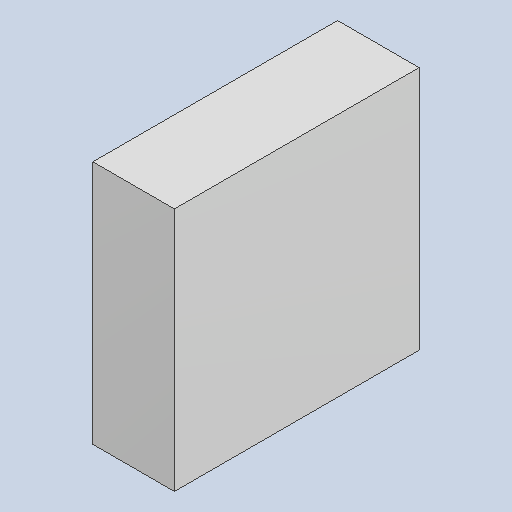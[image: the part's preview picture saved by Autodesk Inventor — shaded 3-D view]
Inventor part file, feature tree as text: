
AUTODESK INVENTOR PART (.ipt)
format: ipt  version: 2023.4 (Build 274418000, 418)  size: 81,408 bytes
history: native  units: mm
features: extrude x1
ambient origin geometry x8: Origin, YZ Plane, XZ Plane, XY Plane, X Axis, Y Axis, Z Axis, Center Point
bodies: Solid1 (feature_tree)
feature tree (1):
  extrude  "Extruded_7"  [1 undecoded]
note: 1 required parameter value undecoded (feature->parameter linkage not recoverable at this tier; creation-order binding heuristic only, values carry confidence <= 0.55)
